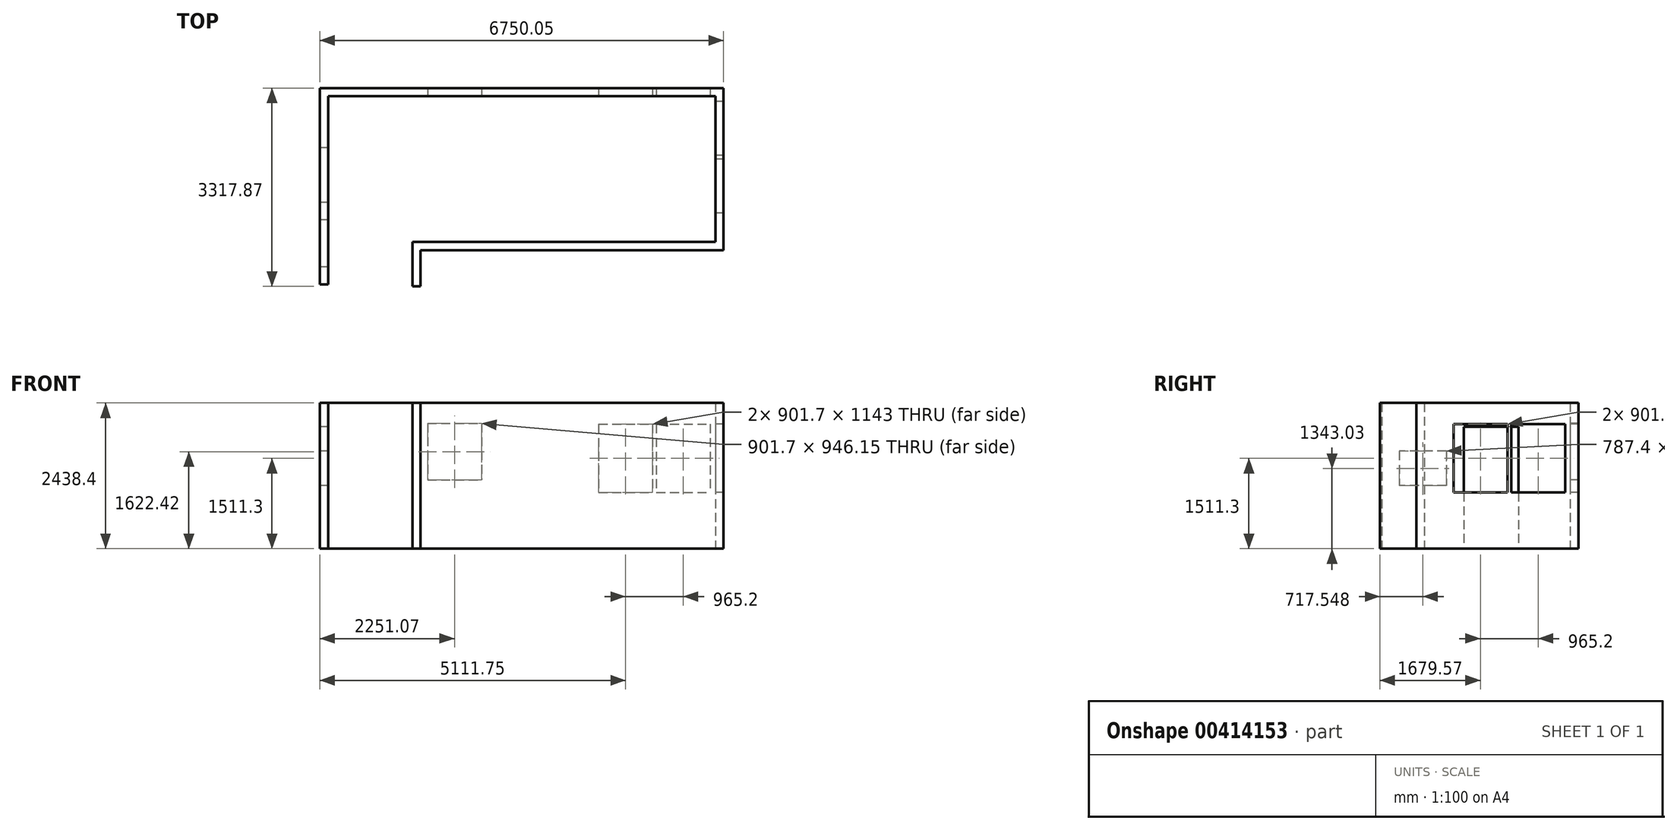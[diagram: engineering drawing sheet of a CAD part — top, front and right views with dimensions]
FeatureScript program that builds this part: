
annotation { "Feature Type Name" : "Feature", "Feature Type Description" : "" }
export const myFeature = defineFeature(function(context is Context, id is Id, definition is map)
    precondition{}
    {
        {
            var Q0;
            Q0=qCreatedBy(makeId("Top.planeOp"),FACE);
            var sketch = newSketch(context, id + "F0", { "sketchPlane" : qUnion([Q0])});
            skLineSegment(sketch, "E0", {"start": v(-1770.7, 2393.7) * mm, "end": v(4706.3, 2393.7) * mm});
            skLineSegment(sketch, "E1", {"start": v(4706.3, 2393.7) * mm, "end": v(4706.3, -44.7) * mm});
            skLineSegment(sketch, "E2", {"start": v(4706.3, -44.7) * mm, "end": v(-361, -44.7) * mm});
            skLineSegment(sketch, "E3", {"start": v(-1907.22, 2530.23) * mm, "end": v(4842.83, 2530.23) * mm});
            skLineSegment(sketch, "E4", {"start": v(4842.83, 2530.23) * mm, "end": v(4842.83, -181.22) * mm});
            skLineSegment(sketch, "E5", {"start": v(-361, -787.64) * mm, "end": v(-361, -44.7) * mm});
            skLineSegment(sketch, "E6", {"start": v(-1770.7, 2393.7) * mm, "end": v(-1770.7, 1530.1) * mm});
            skLineSegment(sketch, "E7", {"start": v(-1770.7, 1530.1) * mm, "end": v(-1907.22, 1530.1) * mm});
            skLineSegment(sketch, "E8", {"start": v(-1770.7, 615.7) * mm, "end": v(-1770.7, -755.9) * mm});
            skLineSegment(sketch, "E9", {"start": v(-1770.7, -755.9) * mm, "end": v(-1907.22, -755.9) * mm});
            skLineSegment(sketch, "E10", {"start": v(-1907.22, -755.9) * mm, "end": v(-1907.22, 615.7) * mm});
            skLineSegment(sketch, "E11", {"start": v(-1907.22, 615.7) * mm, "end": v(-1770.7, 615.7) * mm});
            skLineSegment(sketch, "E12", {"start": v(-361, -787.64) * mm, "end": v(-224.47, -787.64) * mm});
            skLineSegment(sketch, "E13", {"start": v(-224.47, -787.64) * mm, "end": v(-224.47, -181.22) * mm});
            skLineSegment(sketch, "E14", {"start": v(-224.47, -181.22) * mm, "end": v(4842.83, -181.22) * mm});
            skLineSegment(sketch, "E15", {"start": v(-1907.22, 1530.1) * mm, "end": v(-1907.22, 2530.23) * mm});
            skSolve(sketch);
        }
        {
            var Q0;
            Q0 = qSketchRegion(id + "F0", true);
            extrude(context, id + "F1", {"entities" : qUnion([Q0]), "depth" : 2438.4 * mm});
        }
        {
            var Q0;
            Q0=makeQuery(id+"F1.opExtrude","SWEPT_FACE",FACE,{"disambiguationData":[OSD([sQuery(id+"F0.wireOp",EDGE,"E0")])]});
            var sketch = newSketch(context, id + "F2", { "sketchPlane" : qUnion([Q0])});
            skLineSegment(sketch, "E16.bottom", {"start": v(-107, 2095.5) * mm, "end": v(794.7, 2095.5) * mm});
            skLineSegment(sketch, "E16.top", {"start": v(-107, 1149.35) * mm, "end": v(794.7, 1149.35) * mm});
            skLineSegment(sketch, "E16.left", {"start": v(-107, 2095.5) * mm, "end": v(-107, 1149.35) * mm});
            skLineSegment(sketch, "E16.right", {"start": v(794.7, 2095.5) * mm, "end": v(794.7, 1149.35) * mm});
            skLineSegment(sketch, "E17.bottom", {"start": v(2753.68, 2082.8) * mm, "end": v(3655.38, 2082.8) * mm});
            skLineSegment(sketch, "E17.top", {"start": v(2753.68, 939.8) * mm, "end": v(3655.38, 939.8) * mm});
            skLineSegment(sketch, "E17.left", {"start": v(2753.68, 2082.8) * mm, "end": v(2753.68, 939.8) * mm});
            skLineSegment(sketch, "E17.right", {"start": v(3655.38, 2082.8) * mm, "end": v(3655.38, 939.8) * mm});
            skLineSegment(sketch, "E18.bottom", {"start": v(3718.88, 2082.8) * mm, "end": v(4620.58, 2082.8) * mm});
            skLineSegment(sketch, "E18.top", {"start": v(3718.88, 939.8) * mm, "end": v(4620.58, 939.8) * mm});
            skLineSegment(sketch, "E18.left", {"start": v(3718.88, 2082.8) * mm, "end": v(3718.88, 939.8) * mm});
            skLineSegment(sketch, "E18.right", {"start": v(4620.58, 2082.8) * mm, "end": v(4620.58, 939.8) * mm});
            skSolve(sketch);
        }
        {
            var Q0;
            Q0 = qSketchRegion(id + "F2", true);
            extrude(context, id + "F3", {"entities" : qUnion([Q0]), "operationType" : NewBodyOperationType.REMOVE, "endBound" : BoundingType.UP_TO_NEXT, "oppositeDirection" : true, "depth" : 25.4 * mm});
        }
        {
            var Q0;
            Q0=makeQuery(id+"F1.opExtrude","SWEPT_FACE",FACE,{"disambiguationData":[OSD([sQuery(id+"F0.wireOp",EDGE,"E1")])]});
            var sketch = newSketch(context, id + "F4", { "sketchPlane" : qUnion([Q0])});
            skLineSegment(sketch, "E19.bottom", {"start": v(-2307.98, 2082.8) * mm, "end": v(-1406.28, 2082.8) * mm});
            skLineSegment(sketch, "E19.top", {"start": v(-2307.98, 939.8) * mm, "end": v(-1406.28, 939.8) * mm});
            skLineSegment(sketch, "E19.left", {"start": v(-2307.98, 2082.8) * mm, "end": v(-2307.98, 939.8) * mm});
            skLineSegment(sketch, "E19.right", {"start": v(-1406.28, 2082.8) * mm, "end": v(-1406.28, 939.8) * mm});
            skLineSegment(sketch, "E20.bottom", {"start": v(-1342.78, 2082.8) * mm, "end": v(-441.08, 2082.8) * mm});
            skLineSegment(sketch, "E20.top", {"start": v(-1342.78, 939.8) * mm, "end": v(-441.08, 939.8) * mm});
            skLineSegment(sketch, "E20.left", {"start": v(-1342.78, 2082.8) * mm, "end": v(-1342.78, 939.8) * mm});
            skLineSegment(sketch, "E20.right", {"start": v(-441.08, 2082.8) * mm, "end": v(-441.08, 939.8) * mm});
            skSolve(sketch);
        }
        {
            var Q0;
            Q0 = qSketchRegion(id + "F4", true);
            extrude(context, id + "F5", {"entities" : qUnion([Q0]), "operationType" : NewBodyOperationType.REMOVE, "endBound" : BoundingType.UP_TO_NEXT, "oppositeDirection" : true, "depth" : 25.4 * mm});
        }
        {
            var Q0;
            Q0=makeQuery(id+"F1.opExtrude","SWEPT_FACE",FACE,{"disambiguationData":[OSD([sQuery(id+"F0.wireOp",EDGE,"E15")])]});
            var sketch = newSketch(context, id + "F6", { "sketchPlane" : qUnion([Q0])});
            skLineSegment(sketch, "E21.bottom", {"start": v(-1530.1, 2438.4) * mm, "end": v(-615.7, 2438.4) * mm});
            skLineSegment(sketch, "E21.top", {"start": v(-1530.1, 2038.35) * mm, "end": v(-615.7, 2038.35) * mm});
            skLineSegment(sketch, "E21.left", {"start": v(-1530.1, 2438.4) * mm, "end": v(-1530.1, 2038.35) * mm});
            skLineSegment(sketch, "E21.right", {"start": v(-615.7, 2438.4) * mm, "end": v(-615.7, 2038.35) * mm});
            skSolve(sketch);
        }
        {
            var Q0;
            Q0=makeQuery(id+"F6.imprint","IMPRINT",FACE,{"disambiguationData":[TD([[makeQuery(id+"F6.imprint","IMPRINT",EDGE,{"derivedFrom":sQuery(id+"F6.wireOp",EDGE,"E21.bottom")}),-1.0]])]});
            extrude(context, id + "F7", {"entities" : qUnion([Q0]), "operationType" : NewBodyOperationType.ADD, "oppositeDirection" : true, "depth" : 136.53 * mm});
        }
        {
            var Q0;
            Q0=makeQuery(id+"F7.boolean.opBoolean","MERGE",FACE,{"derivedFrom":[makeQuery(id+"F1.opExtrude","SWEPT_FACE",FACE,{"disambiguationData":[OSD([sQuery(id+"F0.wireOp",EDGE,"E10")])]}),makeQuery(id+"F1.opExtrude","SWEPT_FACE",FACE,{"disambiguationData":[OSD([sQuery(id+"F0.wireOp",EDGE,"E15")])]}),makeQuery(id+"F7.opExtrude","CAP_FACE",FACE,{"disambiguationData":[OSD([sQuery(id+"F6.wireOp",EDGE,"E21.bottom"),sQuery(id+"F6.wireOp",EDGE,"E21.top"),sQuery(id+"F6.wireOp",EDGE,"E21.left"),sQuery(id+"F6.wireOp",EDGE,"E21.right")])],"isStart":true})]});
            var sketch = newSketch(context, id + "F8", { "sketchPlane" : qUnion([Q0])});
            skLineSegment(sketch, "E22.bottom", {"start": v(-323.6, 1631.95) * mm, "end": v(463.8, 1631.95) * mm});
            skLineSegment(sketch, "E22.top", {"start": v(-323.6, 1054.1) * mm, "end": v(463.8, 1054.1) * mm});
            skLineSegment(sketch, "E22.left", {"start": v(-323.6, 1631.95) * mm, "end": v(-323.6, 1054.1) * mm});
            skLineSegment(sketch, "E22.right", {"start": v(463.8, 1631.95) * mm, "end": v(463.8, 1054.1) * mm});
            skSolve(sketch);
        }
        {
            var Q0;
            Q0 = qSketchRegion(id + "F8", true);
            extrude(context, id + "F9", {"entities" : qUnion([Q0]), "operationType" : NewBodyOperationType.REMOVE, "endBound" : BoundingType.UP_TO_NEXT, "oppositeDirection" : true, "depth" : 25.4 * mm});
        }
    });
